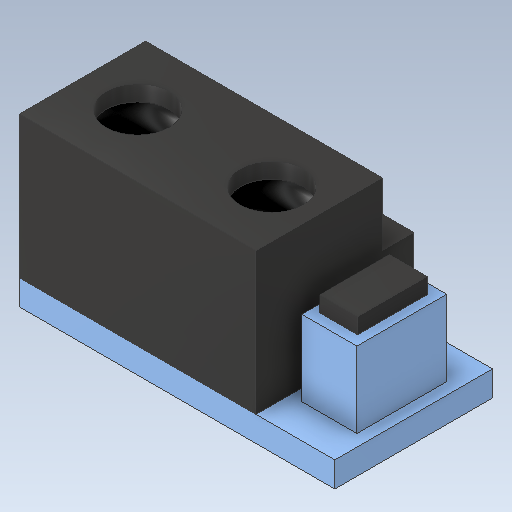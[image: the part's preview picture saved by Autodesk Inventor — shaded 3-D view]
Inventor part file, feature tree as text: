
AUTODESK INVENTOR PART (.ipt)
format: ipt  version: 2020 (Build 240168000, 168)  size: 231,424 bytes
history: native  units: mm
features: sketch x7, extrude x6, plane x4, other x1
ambient origin geometry x8: Origin, YZ Plane, XZ Plane, XY Plane, X Axis, Y Axis, Z Axis, Center Point
bodies: Solid2 (feature_tree)
feature tree (18):
  other  "Bryła1"
  extrude  "Wyciągnięcie proste1"  Depth=15.0mm
  extrude  "Wyciągnięcie proste2"  Depth=5.0mm
  extrude  "Wyciągnięcie proste3"  Depth=8.0mm
  extrude  "Extrusion4"  Depth=4.0mm
  extrude  "Extrusion5"  Depth=3.5mm
  extrude  "Extrusion7"  Depth=4.0mm
  plane  "Work Plane1"
  plane  "Work Plane2"
  plane  "Work Plane3"
  plane  "Work Plane4"
  sketch  "Sketch9"  dims[d7=4.0mm d8=0.0mm d9=4.0mm d10=3.5mm d11=4.0mm d12=3.0mm d13=4.0mm d14=4.0mm d15=1.0mm d16=0.0mm d17=1.6mm d18=0.0mm d19=20.0mm d20=3.5mm d21=5.7mm d22=2.15mm d23=0.75mm d24=4.8mm d25=0.0mm d32=4.4mm d33=0.65mm d34=2.4mm d35=0.5mm d36=1.0mm d37=0.0mm d38=-2.0mm d45=-1.0mm d46=-1.0mm d47=0.4mm d48=0.0mm d49=1.0mm d50=3.054326mm d51=6.108652mm d53=3.0mm d86=-5.0mm d54=0.872665mm d55=0.872665mm d83=0.5mm d84=0.872665mm d85=0.5mm d87=0.872665mm d88=0.5mm d89=0.872665mm]
  sketch  "Szkic1"
  sketch  "Szkic2"
  sketch  "Szkic3"
  sketch  "Sketch4"  dims[d0=10.0mm d1=15.0mm]
  sketch  "Sketch5"  dims[d2=5.0mm d3=7.5mm]
  sketch  "Sketch7"  dims[d4=5.0mm d5=0.0mm d6=8.0mm]
